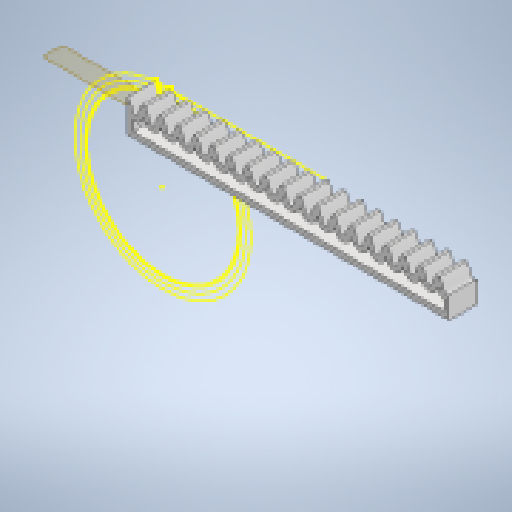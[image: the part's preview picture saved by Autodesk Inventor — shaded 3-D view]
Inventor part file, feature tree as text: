
AUTODESK INVENTOR PART (.ipt)
format: ipt  version: 2023 (Build 270158000, 158)  size: 533,504 bytes
history: native  units: mm
features: other x7, sketch x2, extrude x2, pattern_linear x1, shell x1, reference x1
ambient origin geometry x8: Origin, YZ Plane, XZ Plane, XY Plane, X Axis, Y Axis, Z Axis, Center Point
bodies: Body1 (feature_tree)
feature tree (14):
  other  "rack_V6.ipt"
  other  "Midplane"
  sketch  "Sketch2"  dims[d7=61.768mm d9=2.0mm d10=2.0mm d11=1.0mm d12=5.5mm d13=1.0mm d14=6.5mm d15=0.0mm d16=2.0mm d17=0.0mm d19=0.0mm d20=100.0mm d22=6.283mm d3=20.0mm d4=10.0mm d5=0.0mm d6=10.0mm d8=0.0mm d18=300.0mm d23=6.283mm d24=2.0mm]
  extrude  "Extrusion1"  Depth=20.0mm
  extrude  "Extrusion2"  Depth=10.0mm TaperAngle=0.0deg
  pattern_linear  "Rectangular Pattern1"  Spacing1=10.0mm  [1 undecoded]
  shell  "Shell1"  Thickness=300.0mm
  other  "Solid3::rack_V6.ipt"
  other  "TaggingFeature1"
  sketch  "Sketch1"  dims[d0=10.0mm]
  reference  "Reference1"
  parser-record x1  (decoder bookkeeping rows leaked as tree rows — omitted from the tree; the rows remain in map.json)
  other  "Assembly_V7.iam"
  other  "moulding:1"
note: 1 required parameter value undecoded (feature->parameter linkage not recoverable at this tier; creation-order binding heuristic only, values carry confidence <= 0.55)
note: 1 file-system path scrubbed to <path> (originals preserved in map.json)
